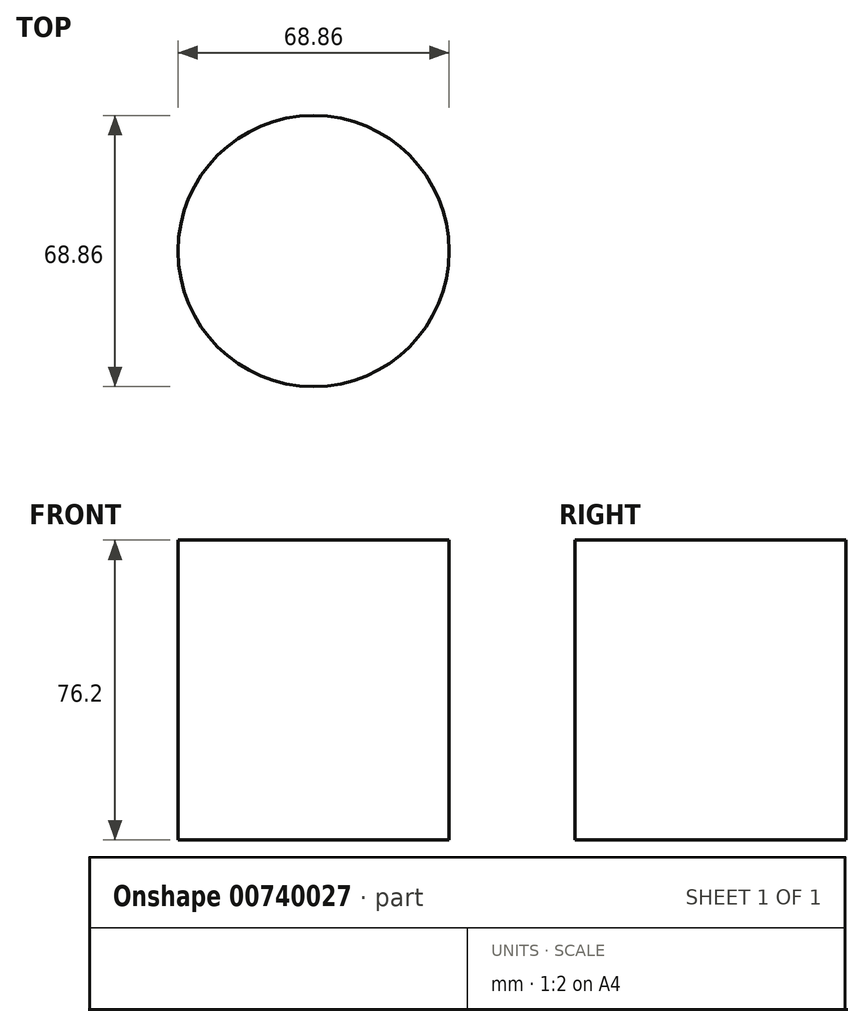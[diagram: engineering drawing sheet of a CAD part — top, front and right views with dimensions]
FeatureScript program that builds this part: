
annotation { "Feature Type Name" : "Feature", "Feature Type Description" : "" }
export const myFeature = defineFeature(function(context is Context, id is Id, definition is map)
    precondition{}
    {
        {
            var Q0;
            Q0=qCreatedBy(makeId("Top.planeOp"),FACE);
            var sketch = newSketch(context, id + "F0", { "sketchPlane" : qUnion([Q0])});
            skCircle(sketch, "E0", {"center": v(0, 0) * mm, "radius": 34.43 * mm});
            skSolve(sketch);
        }
        {
            var Q0;
            Q0=makeQuery(id+"F0.imprint","IMPRINT",FACE,{"disambiguationData":[TD([[makeQuery(id+"F0.imprint","IMPRINT",EDGE,{"derivedFrom":sQuery(id+"F0.wireOp",EDGE,"E0")}),1.0]])]});
            extrude(context, id + "F1", {"entities" : qUnion([Q0]), "depth" : 76.2 * mm, "offsetDistance" : 25.4 * mm});
        }
    });
